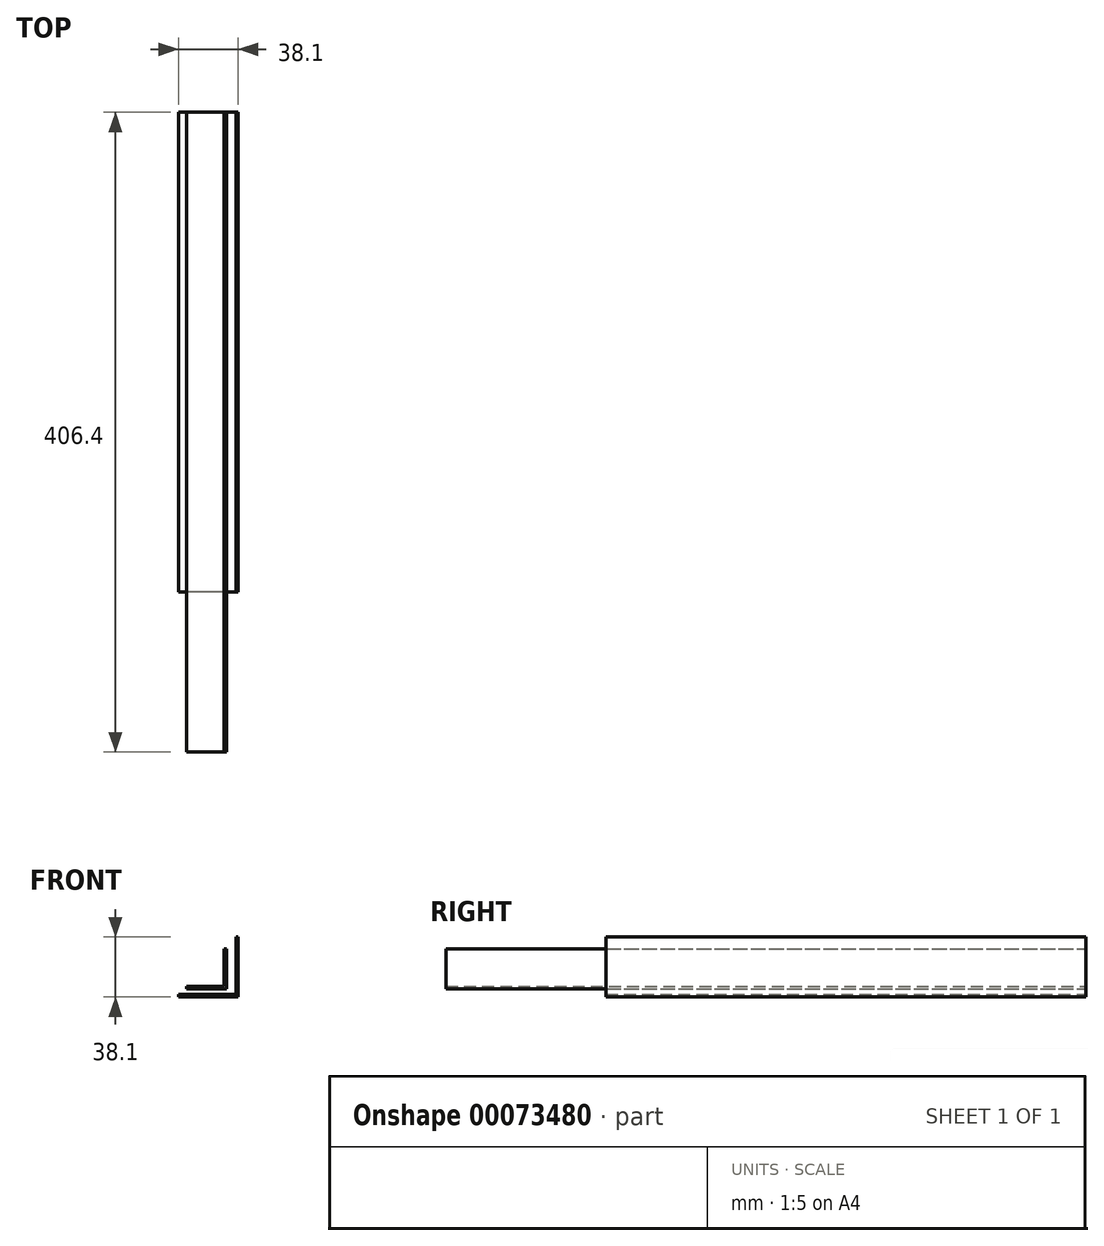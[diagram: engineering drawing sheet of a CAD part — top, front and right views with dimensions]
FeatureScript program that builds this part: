
annotation { "Feature Type Name" : "Feature", "Feature Type Description" : "" }
export const myFeature = defineFeature(function(context is Context, id is Id, definition is map)
    precondition{}
    {
        {
            var Q0;
            Q0=qCreatedBy(makeId("Front.planeOp"),FACE);
            var sketch = newSketch(context, id + "F0", { "sketchPlane" : qUnion([Q0])});
            skLineSegment(sketch, "E0.rect.bottom", {"start": v(12.7, 0.8) * mm, "end": v(-12.7, 0.8) * mm});
            skLineSegment(sketch, "E0.rect.top", {"start": v(12.7, -0.8) * mm, "end": v(-12.7, -0.8) * mm});
            skLineSegment(sketch, "E0.rect.left", {"start": v(12.7, 0.8) * mm, "end": v(12.7, -0.8) * mm});
            skLineSegment(sketch, "E0.rect.right", {"start": v(-12.7, 0.8) * mm, "end": v(-12.7, -0.8) * mm});
            skPoint(sketch, "E0.rect.middle", {"position": v(0, 0) * mm});
            skLineSegment(sketch, "E1.bottom", {"start": v(12.7, -0.8) * mm, "end": v(11.11, -0.8) * mm});
            skLineSegment(sketch, "E1.top", {"start": v(12.7, 24.6) * mm, "end": v(11.11, 24.6) * mm});
            skLineSegment(sketch, "E1.left", {"start": v(12.7, -0.8) * mm, "end": v(12.7, 24.6) * mm});
            skLineSegment(sketch, "E1.right", {"start": v(11.11, -0.8) * mm, "end": v(11.11, 24.6) * mm});
            skSolve(sketch);
        }
        {
            var Q0;
            Q0=qSketchRegion(id+"F0",true);
            extrude(context, id + "F1", {"entities" : qUnion([Q0]), "depth" : 406.4 * mm});
        }
        {
            var Q0;
            Q0=qCreatedBy(makeId("Front.planeOp"),FACE);
            var sketch = newSketch(context, id + "F2", { "sketchPlane" : qUnion([Q0])});
            skLineSegment(sketch, "E2.rect.bottom", {"start": v(20.1, -4.5) * mm, "end": v(-18, -4.5) * mm});
            skLineSegment(sketch, "E2.rect.top", {"start": v(20.1, -6.09) * mm, "end": v(-18, -6.09) * mm});
            skLineSegment(sketch, "E2.rect.left", {"start": v(20.1, -4.5) * mm, "end": v(20.1, -6.09) * mm});
            skLineSegment(sketch, "E2.rect.right", {"start": v(-18, -4.5) * mm, "end": v(-18, -6.09) * mm});
            skPoint(sketch, "E2.rect.middle", {"position": v(1.06, -5.3) * mm});
            skLineSegment(sketch, "E3.bottom", {"start": v(20.1, -6.09) * mm, "end": v(18.52, -6.09) * mm});
            skLineSegment(sketch, "E3.top", {"start": v(20.1, 32.01) * mm, "end": v(18.52, 32.01) * mm});
            skLineSegment(sketch, "E3.left", {"start": v(20.1, -6.09) * mm, "end": v(20.1, 32.01) * mm});
            skLineSegment(sketch, "E3.right", {"start": v(18.52, -6.09) * mm, "end": v(18.52, 32.01) * mm});
            skSolve(sketch);
        }
        {
            var Q0;
            Q0=qSketchRegion(id+"F2",true);
            extrude(context, id + "F3", {"entities" : qUnion([Q0]), "depth" : 304.8 * mm});
        }
    });
